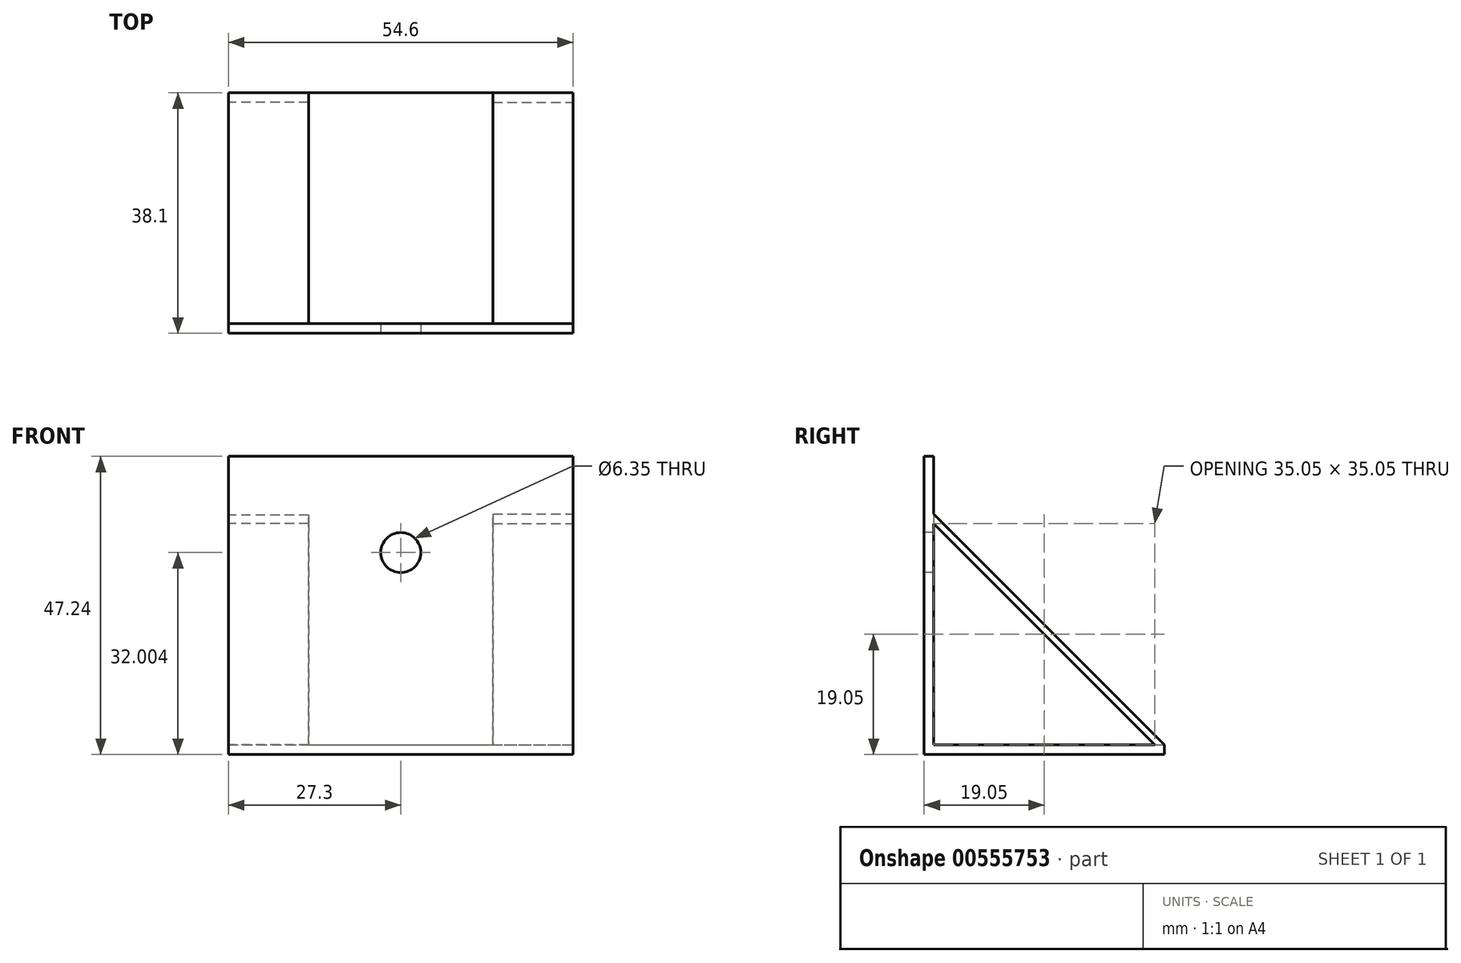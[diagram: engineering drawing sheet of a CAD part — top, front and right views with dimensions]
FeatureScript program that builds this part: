
annotation { "Feature Type Name" : "Feature", "Feature Type Description" : "" }
export const myFeature = defineFeature(function(context is Context, id is Id, definition is map)
    precondition{}
    {
        {
            var Q0;
            Q0=qCreatedBy(makeId("Top.planeOp"),FACE);
            var sketch = newSketch(context, id + "F0", { "sketchPlane" : qUnion([Q0])});
            skLineSegment(sketch, "E0.bottom", {"start": v(-27.3, -19.05) * mm, "end": v(27.3, -19.05) * mm});
            skLineSegment(sketch, "E0.top", {"start": v(-27.3, 19.05) * mm, "end": v(27.3, 19.05) * mm});
            skLineSegment(sketch, "E0.left", {"start": v(-27.3, -19.05) * mm, "end": v(-27.3, 19.05) * mm});
            skLineSegment(sketch, "E0.right", {"start": v(27.3, -19.05) * mm, "end": v(27.3, 19.05) * mm});
            skPoint(sketch, "E0.middle", {"position": v(0, 0) * mm});
            skSolve(sketch);
        }
        {
            var Q0;
            Q0 = qSketchRegion(id + "F0", true);
            extrude(context, id + "F1", {"entities" : qUnion([Q0]), "depth" : 1.52 * mm, "offsetDistance" : 25.4 * mm});
        }
        {
            var Q0;
            Q0=makeQuery(id+"F1.opExtrude","CAP_FACE",FACE,{"disambiguationData":[OSD([sQuery(id+"F0.wireOp",EDGE,"E0.bottom"),sQuery(id+"F0.wireOp",EDGE,"E0.top"),sQuery(id+"F0.wireOp",EDGE,"E0.left"),sQuery(id+"F0.wireOp",EDGE,"E0.right")])],"isStart":false});
            var sketch = newSketch(context, id + "F2", { "sketchPlane" : qUnion([Q0])});
            skLineSegment(sketch, "E1.bottom", {"start": v(-27.3, -19.05) * mm, "end": v(27.3, -19.05) * mm});
            skLineSegment(sketch, "E1.top", {"start": v(-27.3, -17.53) * mm, "end": v(27.3, -17.53) * mm});
            skLineSegment(sketch, "E1.left", {"start": v(-27.3, -19.05) * mm, "end": v(-27.3, -17.53) * mm});
            skLineSegment(sketch, "E1.right", {"start": v(27.3, -19.05) * mm, "end": v(27.3, -17.53) * mm});
            skSolve(sketch);
        }
        {
            var Q0;
            Q0 = qSketchRegion(id + "F2", true);
            extrude(context, id + "F3", {"entities" : qUnion([Q0]), "operationType" : NewBodyOperationType.ADD, "depth" : 45.72 * mm, "offsetDistance" : 25.4 * mm});
        }
        {
            var Q0;
            Q0=makeQuery(id+"F3.boolean.opBoolean","MERGE",FACE,{"derivedFrom":[makeQuery(id+"F1.opExtrude","SWEPT_FACE",FACE,{"disambiguationData":[OSD([sQuery(id+"F0.wireOp",EDGE,"E0.bottom")])]}),makeQuery(id+"F3.opExtrude","SWEPT_FACE",FACE,{"disambiguationData":[OSD([sQuery(id+"F2.wireOp",EDGE,"E1.bottom")])]})]});
            var sketch = newSketch(context, id + "F4", { "sketchPlane" : qUnion([Q0])});
            skCircle(sketch, "E2", {"center": v(0, 32) * mm, "radius": 3.17 * mm});
            skSolve(sketch);
        }
        {
            var Q0;
            Q0 = qSketchRegion(id + "F4", true);
            extrude(context, id + "F5", {"entities" : qUnion([Q0]), "operationType" : NewBodyOperationType.REMOVE, "oppositeDirection" : true, "depth" : 25.4 * mm, "offsetDistance" : 25.4 * mm});
        }
        {
            var Q0;
            Q0=makeQuery(id+"F3.boolean.opBoolean","MERGE",FACE,{"derivedFrom":[makeQuery(id+"F1.opExtrude","SWEPT_FACE",FACE,{"disambiguationData":[OSD([sQuery(id+"F0.wireOp",EDGE,"E0.right")])]}),makeQuery(id+"F3.opExtrude","SWEPT_FACE",FACE,{"disambiguationData":[OSD([sQuery(id+"F2.wireOp",EDGE,"E1.right")])]})]});
            var sketch = newSketch(context, id + "F6", { "sketchPlane" : qUnion([Q0])});
            skLineSegment(sketch, "E3", {"start": v(19.05, 1.52) * mm, "end": v(-17.53, 38.1) * mm});
            skLineSegment(sketch, "E4", {"start": v(-17.53, 38.1) * mm, "end": v(-17.53, 36.58) * mm});
            skLineSegment(sketch, "E5", {"start": v(-17.53, 36.58) * mm, "end": v(17.53, 1.52) * mm});
            skLineSegment(sketch, "E6", {"start": v(17.53, 1.52) * mm, "end": v(19.05, 1.52) * mm});
            skSolve(sketch);
        }
        {
            var Q0;
            Q0 = qSketchRegion(id + "F6", true);
            extrude(context, id + "F7", {"entities" : qUnion([Q0]), "operationType" : NewBodyOperationType.ADD, "oppositeDirection" : true, "depth" : 12.7 * mm, "offsetDistance" : 25.4 * mm});
        }
        {
            var Q0;
            Q0=makeQuery(id+"F3.boolean.opBoolean","MERGE",FACE,{"derivedFrom":[makeQuery(id+"F1.opExtrude","SWEPT_FACE",FACE,{"disambiguationData":[OSD([sQuery(id+"F0.wireOp",EDGE,"E0.left")])]}),makeQuery(id+"F3.opExtrude","SWEPT_FACE",FACE,{"disambiguationData":[OSD([sQuery(id+"F2.wireOp",EDGE,"E1.left")])]})]});
            var sketch = newSketch(context, id + "F8", { "sketchPlane" : qUnion([Q0])});
            skLineSegment(sketch, "E7", {"start": v(-19.05, 1.52) * mm, "end": v(17.53, 37.92) * mm});
            skLineSegment(sketch, "E8", {"start": v(17.53, 37.92) * mm, "end": v(17.53, 36.58) * mm});
            skLineSegment(sketch, "E9", {"start": v(17.53, 36.58) * mm, "end": v(-17.53, 1.52) * mm});
            skLineSegment(sketch, "E10", {"start": v(-17.53, 1.52) * mm, "end": v(-19.05, 1.52) * mm});
            skSolve(sketch);
        }
        {
            var Q0;
            Q0 = qSketchRegion(id + "F8", true);
            extrude(context, id + "F9", {"entities" : qUnion([Q0]), "operationType" : NewBodyOperationType.ADD, "oppositeDirection" : true, "depth" : 12.7 * mm, "offsetDistance" : 25.4 * mm});
        }
    });
